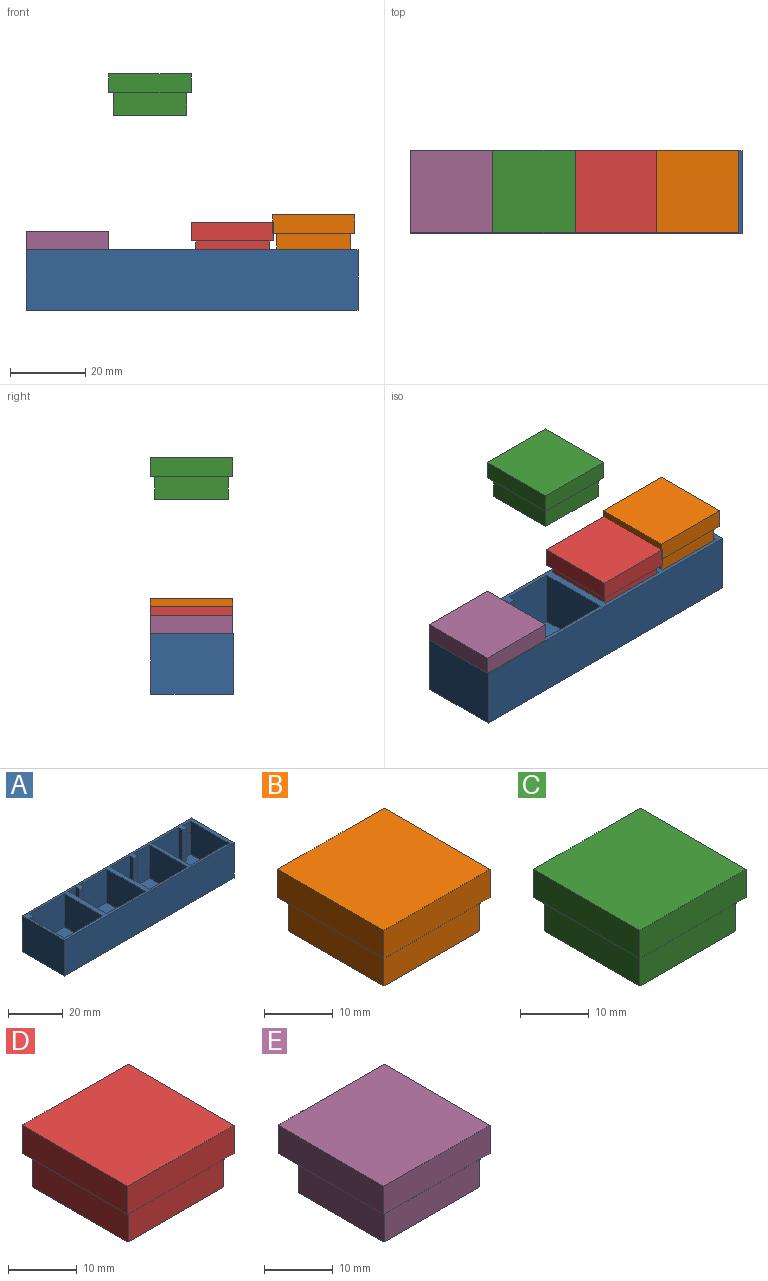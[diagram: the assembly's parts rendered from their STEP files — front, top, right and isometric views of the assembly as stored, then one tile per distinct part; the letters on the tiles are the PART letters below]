
ASSEMBLY  parts=5 mates=4
PART A: 40 faces, bbox 88x22x16 mm
  f0: plane 20x15mm, normal (0,1,0), area 300mm2, adj f1,f33,f34,f38
  f1: plane 20x15mm, normal (1,0,0), area 300mm2, adj f0,f2,f34,f38
  f2: plane 15x10mm, normal (0,-1,0), area 150mm2, adj f1,f3,f34,f38
  f3: plane 15x2mm, normal (-1,0,0), area 30mm2, adj f2,f4,f34,f38
  f4: plane 15x2mm, normal (0,-1,0), area 30mm2, adj f3,f5,f34,f38
  f5: plane 15x2mm, normal (1,0,0), area 30mm2, adj f4,f6,f34,f38
  f6: plane 15x8mm, normal (0,-1,0), area 120mm2, adj f5,f33,f34,f38
  f7: plane 20x15mm, normal (0,1,0), area 300mm2, adj f8,f29,f34,f39
  f8: plane 20x15mm, normal (1,0,0), area 300mm2, adj f7,f9,f34,f39
  f9: plane 15x14mm, normal (0,-1,0), area 210mm2, adj f8,f10,f34,f39
  f10: plane 15x2mm, normal (-1,0,0), area 30mm2, adj f9,f11,f34,f39
  f11: plane 15x2mm, normal (0,-1,0), area 30mm2, adj f10,f12,f34,f39
  f12: plane 15x2mm, normal (1,0,0), area 30mm2, adj f11,f13,f34,f39
  f13: plane 15x4mm, normal (0,-1,0), area 60mm2, adj f12,f29,f34,f39
  f14: plane 20x15mm, normal (0,1,0), area 300mm2, adj f15,f30,f34,f37
  f15: plane 20x15mm, normal (1,0,0), area 300mm2, adj f14,f16,f34,f37
  f16: plane 15x4mm, normal (0,-1,0), area 60mm2, adj f15,f17,f34,f37
  f17: plane 15x2mm, normal (-1,0,0), area 30mm2, adj f16,f18,f34,f37
  f18: plane 15x2mm, normal (0,-1,0), area 30mm2, adj f17,f19,f34,f37
  f19: plane 15x2mm, normal (1,0,0), area 30mm2, adj f18,f20,f34,f37
  f20: plane 15x14mm, normal (0,-1,0), area 210mm2, adj f19,f30,f34,f37
  f21: plane 22x16mm, normal (-1,0,0), area 352mm2, adj f22,f31,f34,f35
  f22: plane 88x16mm, normal (0,-1,0), area 1408mm2, adj f21,f23,f34,f35
  f23: plane 22x16mm, normal (1,0,0), area 352mm2, adj f22,f31,f34,f35
  f24: plane 20x15mm, normal (0,1,0), area 300mm2, adj f25,f32,f34,f36
  f25: plane 18x15mm, normal (1,0,0), area 270mm2, adj f24,f26,f34,f36
  f26: plane 15x2mm, normal (0,-1,0), area 30mm2, adj f25,f27,f34,f36
  f27: plane 15x2mm, normal (1,0,0), area 30mm2, adj f26,f28,f34,f36
  f28: plane 18x15mm, normal (0,-1,0), area 270mm2, adj f27,f32,f34,f36
  f29: plane 20x15mm, normal (-1,0,0), area 300mm2, adj f7,f13,f34,f39
  f30: plane 20x15mm, normal (-1,0,0), area 300mm2, adj f14,f20,f34,f37
  f31: plane 88x16mm, normal (0,1,0), area 1408mm2, adj f21,f23,f34,f35
  f32: plane 20x15mm, normal (-1,0,0), area 300mm2, adj f24,f28,f34,f36
  f33: plane 20x15mm, normal (-1,0,0), area 300mm2, adj f0,f6,f34,f38
  f34: plane 88x22mm, normal (0,0,1), area 352mm2, adj f0,f1,f2,f3,f4,f5,f6,f7
  f35: plane 88x22mm, normal (0,0,-1), area 1936mm2, adj f21,f22,f23,f31
  f36: plane 20x20mm, normal (0,0,1), area 396mm2, adj f24,f25,f26,f27,f28,f32
  f37: plane 20x20mm, normal (0,0,1), area 396mm2, adj f14,f15,f16,f17,f18,f19,f20,f30
  f38: plane 20x20mm, normal (0,0,1), area 396mm2, adj f0,f1,f2,f3,f4,f5,f6,f33
  f39: plane 20x20mm, normal (0,0,1), area 396mm2, adj f7,f8,f9,f10,f11,f12,f13,f29
PART B: 24 faces, bbox 21.8x21.8x11 mm
  f0: plane 6x2mm, normal (1,0,0), area 12mm2, adj f1,f15,f16,f17
  f1: plane 6x1.6mm, normal (0,-1,0), area 9.6mm2, adj f0,f2,f16,f17
  f2: plane 17.6x6mm, normal (-1,0,0), area 105.6mm2, adj f1,f3,f16,f17
  f3: plane 17.6x6mm, normal (0,1,0), area 105.6mm2, adj f2,f4,f16,f17
  f4: plane 17.6x6mm, normal (1,0,0), area 105.6mm2, adj f3,f5,f16,f17
  f5: plane 11.6x6mm, normal (0,-1,0), area 69.6mm2, adj f4,f6,f16,f17
  f6: plane 6x2mm, normal (-1,0,0), area 12mm2, adj f5,f15,f16,f17
  f7: plane 19.6x6mm, normal (0,-1,0), area 117.6mm2, adj f8,f14,f16,f23
  f8: plane 19.6x6mm, normal (1,0,0), area 117.6mm2, adj f7,f9,f16,f23
  f9: plane 6x3.6mm, normal (0,1,0), area 21.6mm2, adj f8,f10,f16,f23
  f10: plane 6x2mm, normal (-1,0,0), area 12mm2, adj f9,f11,f16,f23
  f11: plane 6x2.4mm, normal (0,1,0), area 14.4mm2, adj f10,f12,f16,f23
  f12: plane 6x2mm, normal (1,0,0), area 12mm2, adj f11,f13,f16,f23
  f13: plane 13.6x6mm, normal (0,1,0), area 81.6mm2, adj f12,f14,f16,f23
  f14: plane 19.6x6mm, normal (-1,0,0), area 117.6mm2, adj f7,f13,f16,f23
  f15: plane 6x4.4mm, normal (0,-1,0), area 26.4mm2, adj f0,f6,f16,f17
  f16: plane 19.6x19.6mm, normal (0,0,-1), area 78.4mm2, adj f0,f1,f2,f3,f4,f5,f6,f7
  f17: plane 17.6x17.6mm, normal (0,0,-1), area 301mm2, adj f0,f1,f2,f3,f4,f5,f6,f15
  f18: plane 21.8x5mm, normal (1,0,0), area 109mm2, adj f19,f21,f22,f23
  f19: plane 21.8x5mm, normal (0,1,0), area 109mm2, adj f18,f20,f22,f23
  f20: plane 21.8x5mm, normal (-1,0,0), area 109mm2, adj f19,f21,f22,f23
  f21: plane 21.8x5mm, normal (0,-1,0), area 109mm2, adj f18,f20,f22,f23
  f22: plane 21.8x21.8mm, normal (0,0,1), area 475.2mm2, adj f18,f19,f20,f21
  f23: plane 21.8x21.8mm, normal (0,0,-1), area 95.9mm2, adj f7,f8,f9,f10,f11,f12,f13,f14
PART C: 24 faces, bbox 21.8x21.8x11 mm
  f0: plane 17.6x6mm, normal (0,1,0), area 105.6mm2, adj f1,f15,f16,f17
  f1: plane 17.6x6mm, normal (1,0,0), area 105.6mm2, adj f0,f2,f16,f17
  f2: plane 6x1.6mm, normal (0,-1,0), area 9.6mm2, adj f1,f3,f16,f17
  f3: plane 6x2mm, normal (-1,0,0), area 12mm2, adj f2,f4,f16,f17
  f4: plane 6x4.4mm, normal (0,-1,0), area 26.4mm2, adj f3,f5,f16,f17
  f5: plane 6x2mm, normal (1,0,0), area 12mm2, adj f4,f6,f16,f17
  f6: plane 11.6x6mm, normal (0,-1,0), area 69.6mm2, adj f5,f15,f16,f17
  f7: plane 6x2mm, normal (1,0,0), area 12mm2, adj f8,f14,f16,f18
  f8: plane 6x3.6mm, normal (0,1,0), area 21.6mm2, adj f7,f9,f16,f18
  f9: plane 19.6x6mm, normal (-1,0,0), area 117.6mm2, adj f8,f10,f16,f18
  f10: plane 19.6x6mm, normal (0,-1,0), area 117.6mm2, adj f9,f11,f16,f18
  f11: plane 19.6x6mm, normal (1,0,0), area 117.6mm2, adj f10,f12,f16,f18
  f12: plane 13.6x6mm, normal (0,1,0), area 81.6mm2, adj f11,f13,f16,f18
  f13: plane 6x2mm, normal (-1,0,0), area 12mm2, adj f12,f14,f16,f18
  f14: plane 6x2.4mm, normal (0,1,0), area 14.4mm2, adj f7,f13,f16,f18
  f15: plane 17.6x6mm, normal (-1,0,0), area 105.6mm2, adj f0,f6,f16,f17
  f16: plane 19.6x19.6mm, normal (0,0,-1), area 78.4mm2, adj f0,f1,f2,f3,f4,f5,f6,f7
  f17: plane 17.6x17.6mm, normal (0,0,-1), area 301mm2, adj f0,f1,f2,f3,f4,f5,f6,f15
  f18: plane 21.8x21.8mm, normal (0,0,-1), area 95.9mm2, adj f7,f8,f9,f10,f11,f12,f13,f14
  f19: plane 21.8x5mm, normal (1,0,0), area 109mm2, adj f18,f20,f22,f23
  f20: plane 21.8x5mm, normal (0,1,0), area 109mm2, adj f18,f19,f21,f23
  f21: plane 21.8x5mm, normal (-1,0,0), area 109mm2, adj f18,f20,f22,f23
  f22: plane 21.8x5mm, normal (0,-1,0), area 109mm2, adj f18,f19,f21,f23
  f23: plane 21.8x21.8mm, normal (0,0,1), area 475.2mm2, adj f19,f20,f21,f22
PART D: 24 faces, bbox 21.8x21.8x11 mm
  f0: plane 6x2mm, normal (-1,0,0), area 12mm2, adj f1,f15,f16,f17
  f1: plane 6x4.4mm, normal (0,-1,0), area 26.4mm2, adj f0,f2,f16,f17
  f2: plane 6x2mm, normal (1,0,0), area 12mm2, adj f1,f3,f16,f17
  f3: plane 6x5.6mm, normal (0,-1,0), area 33.6mm2, adj f2,f4,f16,f17
  f4: plane 17.6x6mm, normal (-1,0,0), area 105.6mm2, adj f3,f5,f16,f17
  f5: plane 17.6x6mm, normal (0,1,0), area 105.6mm2, adj f4,f6,f16,f17
  f6: plane 17.6x6mm, normal (1,0,0), area 105.6mm2, adj f5,f15,f16,f17
  f7: plane 19.6x6mm, normal (1,0,0), area 117.6mm2, adj f8,f14,f16,f23
  f8: plane 7.6x6mm, normal (0,1,0), area 45.6mm2, adj f7,f9,f16,f23
  f9: plane 6x2mm, normal (-1,0,0), area 12mm2, adj f8,f10,f16,f23
  f10: plane 6x2.4mm, normal (0,1,0), area 14.4mm2, adj f9,f11,f16,f23
  f11: plane 6x2mm, normal (1,0,0), area 12mm2, adj f10,f12,f16,f23
  f12: plane 9.6x6mm, normal (0,1,0), area 57.6mm2, adj f11,f13,f16,f23
  f13: plane 19.6x6mm, normal (-1,0,0), area 117.6mm2, adj f12,f14,f16,f23
  f14: plane 19.6x6mm, normal (0,-1,0), area 117.6mm2, adj f7,f13,f16,f23
  f15: plane 7.6x6mm, normal (0,-1,0), area 45.6mm2, adj f0,f6,f16,f17
  f16: plane 19.6x19.6mm, normal (0,0,-1), area 78.4mm2, adj f0,f1,f2,f3,f4,f5,f6,f7
  f17: plane 17.6x17.6mm, normal (0,0,-1), area 301mm2, adj f0,f1,f2,f3,f4,f5,f6,f15
  f18: plane 21.8x5mm, normal (1,0,0), area 109mm2, adj f19,f21,f22,f23
  f19: plane 21.8x5mm, normal (0,1,0), area 109mm2, adj f18,f20,f22,f23
  f20: plane 21.8x5mm, normal (-1,0,0), area 109mm2, adj f19,f21,f22,f23
  f21: plane 21.8x5mm, normal (0,-1,0), area 109mm2, adj f18,f20,f22,f23
  f22: plane 21.8x21.8mm, normal (0,0,1), area 475.2mm2, adj f18,f19,f20,f21
  f23: plane 21.8x21.8mm, normal (0,0,-1), area 95.9mm2, adj f7,f8,f9,f10,f11,f12,f13,f14
PART E: 20 faces, bbox 21.8x21.8x11 mm
  f0: plane 15.6x6mm, normal (0,-1,0), area 93.6mm2, adj f1,f11,f12,f13
  f1: plane 17.6x6mm, normal (-1,0,0), area 105.6mm2, adj f0,f2,f12,f13
  f2: plane 17.6x6mm, normal (0,1,0), area 105.6mm2, adj f1,f3,f12,f13
  f3: plane 15.6x6mm, normal (1,0,0), area 93.6mm2, adj f2,f4,f12,f13
  f4: plane 6x2mm, normal (0,-1,0), area 12mm2, adj f3,f11,f12,f13
  f5: plane 17.6x6mm, normal (0,1,0), area 105.6mm2, adj f6,f10,f12,f19
  f6: plane 6x2mm, normal (-1,0,0), area 12mm2, adj f5,f7,f12,f19
  f7: plane 6x2mm, normal (0,1,0), area 12mm2, adj f6,f8,f12,f19
  f8: plane 17.6x6mm, normal (-1,0,0), area 105.6mm2, adj f7,f9,f12,f19
  f9: plane 19.6x6mm, normal (0,-1,0), area 117.6mm2, adj f8,f10,f12,f19
  f10: plane 19.6x6mm, normal (1,0,0), area 117.6mm2, adj f5,f9,f12,f19
  f11: plane 6x2mm, normal (1,0,0), area 12mm2, adj f0,f4,f12,f13
  f12: plane 19.6x19.6mm, normal (0,0,-1), area 74.4mm2, adj f0,f1,f2,f3,f4,f5,f6,f7
  f13: plane 17.6x17.6mm, normal (0,0,-1), area 305.8mm2, adj f0,f1,f2,f3,f4,f11
  f14: plane 21.8x5mm, normal (-1,0,0), area 109mm2, adj f15,f17,f18,f19
  f15: plane 21.8x5mm, normal (0,-1,0), area 109mm2, adj f14,f16,f18,f19
  f16: plane 21.8x5mm, normal (1,0,0), area 109mm2, adj f15,f17,f18,f19
  f17: plane 21.8x5mm, normal (0,1,0), area 109mm2, adj f14,f16,f18,f19
  f18: plane 21.8x21.8mm, normal (0,0,1), area 475.2mm2, adj f14,f15,f16,f17
  f19: plane 21.8x21.8mm, normal (0,0,-1), area 95.1mm2, adj f5,f6,f7,f8,f9,f10,f14,f15
PLACE A t=(19.25,23.48,-13.69)mm fixed
PLACE B t=(12.4,76.69,6.61)mm
PLACE C t=(40.44,75.74,44.02)mm
PLACE D t=(27.77,76.6,4.67)mm
PLACE E t=(53.85,74.58,2.31)mm
MATE slider C.f16 <-> A.f34  axis (0,0,1) through (4.25,33.48,38.02)mm
MATE slider B.f16 <-> A.f34  axis (0,0,1) through (57.67,33.48,0.61)mm
MATE slider D.f16 <-> A.f34  axis (0,0,1) through (32.25,33.48,-1.33)mm
MATE slider E.f12 <-> A.f34  axis (0,0,1) through (-21.75,31.48,-3.69)mm
